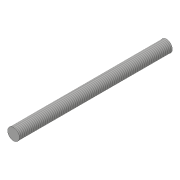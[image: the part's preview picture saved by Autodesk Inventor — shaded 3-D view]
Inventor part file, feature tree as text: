
AUTODESK INVENTOR PART (.ipt)
format: ipt  version: 2017 (Build 210142000, 142)  size: 76,288 bytes
history: native  units: mm
features: extrude x1, thread x1, sketch x1
ambient origin geometry x8: Origin, YZ Plane, XZ Plane, XY Plane, X Axis, Y Axis, Z Axis, Center Point
bodies: Solid1 (feature_tree)
feature tree (3):
  extrude  "Extrusion1"  Depth=130.0mm TaperAngle=0.0deg
  thread  "Thread1"  [1 undecoded]
  sketch  "Sketch1"  dims[d0=10.0mm d1=130.0mm d2=0.0mm d3=10.0mm d4=0.0mm]
note: 1 required parameter value undecoded (feature->parameter linkage not recoverable at this tier; creation-order binding heuristic only, values carry confidence <= 0.55)
